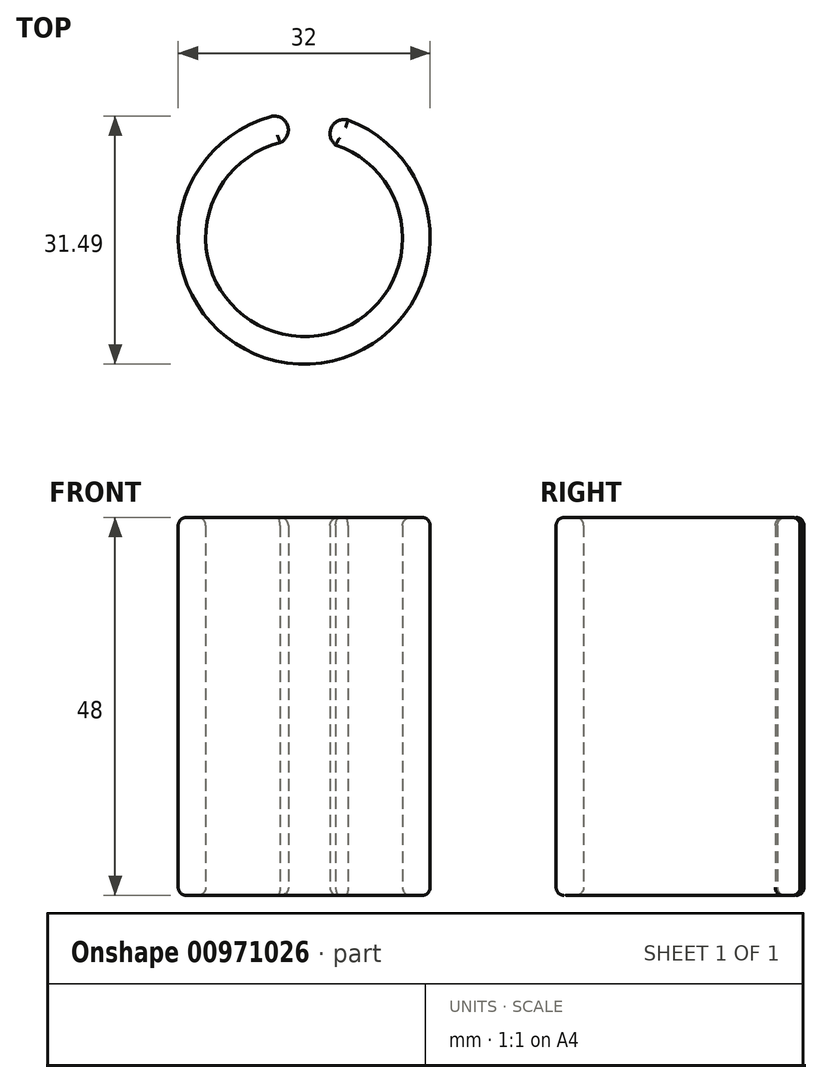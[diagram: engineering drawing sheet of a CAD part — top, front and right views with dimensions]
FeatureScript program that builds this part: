
annotation { "Feature Type Name" : "Feature", "Feature Type Description" : "" }
export const myFeature = defineFeature(function(context is Context, id is Id, definition is map)
    precondition{}
    {
        {
            var Q0;
            Q0=qCreatedBy(makeId("Top.planeOp"),FACE);
            var sketch = newSketch(context, id + "F0", { "sketchPlane" : qUnion([Q0])});
            skArc(sketch, "E0", {"start": v(-3.07, 12.12) * mm, "mid": v(-0.49, -12.5) * mm, "end": v(4, 11.84) * mm});
            skArc(sketch, "E1", {"start": v(-4.23, 15.43) * mm, "mid": v(-0.7, -15.98) * mm, "end": v(5.57, 15) * mm});
            skArc(sketch, "E2", {"start": v(5.57, 15) * mm, "mid": v(3.47, 14.07) * mm, "end": v(4, 11.84) * mm});
            skArc(sketch, "E3", {"start": v(-3.07, 12.12) * mm, "mid": v(-2.1, 14.32) * mm, "end": v(-4.23, 15.43) * mm});
            skSolve(sketch);
        }
        {
            var Q0;
            Q0=makeQuery(id+"F0.imprint","IMPRINT",FACE,{"disambiguationData":[TD([[makeQuery(id+"F0.imprint","IMPRINT",EDGE,{"derivedFrom":sQuery(id+"F0.wireOp",EDGE,"E0")}),-1.0]])]});
            extrude(context, id + "F1", {"entities" : qUnion([Q0]), "depth" : 48 * mm, "offsetDistance" : 25 * mm, "symmetric" : true});
        }
        {
            var Q0;
            Q0=makeQuery(id+"F1.opExtrude","CAP_EDGE",EDGE,{"disambiguationData":[OSD([sQuery(id+"F0.wireOp",EDGE,"E1")])],"isStart":false});
            var Q1;
            Q1=makeQuery(id+"F1.opExtrude","CAP_EDGE",EDGE,{"disambiguationData":[OSD([sQuery(id+"F0.wireOp",EDGE,"E0")])],"isStart":false});
            var Q2;
            Q2=makeQuery(id+"F1.opExtrude","CAP_EDGE",EDGE,{"disambiguationData":[OSD([sQuery(id+"F0.wireOp",EDGE,"E3")])],"isStart":false});
            var Q3;
            Q3=makeQuery(id+"F1.opExtrude","CAP_EDGE",EDGE,{"disambiguationData":[OSD([sQuery(id+"F0.wireOp",EDGE,"E2")])],"isStart":false});
            var Q4;
            Q4=makeQuery(id+"F1.opExtrude","CAP_EDGE",EDGE,{"disambiguationData":[OSD([sQuery(id+"F0.wireOp",EDGE,"E0")])],"isStart":true});
            var Q5;
            Q5=makeQuery(id+"F1.opExtrude","CAP_EDGE",EDGE,{"disambiguationData":[OSD([sQuery(id+"F0.wireOp",EDGE,"E2")])],"isStart":true});
            var Q6;
            Q6=makeQuery(id+"F1.opExtrude","CAP_EDGE",EDGE,{"disambiguationData":[OSD([sQuery(id+"F0.wireOp",EDGE,"E3")])],"isStart":true});
            var Q7;
            Q7=makeQuery(id+"F1.opExtrude","CAP_EDGE",EDGE,{"disambiguationData":[OSD([sQuery(id+"F0.wireOp",EDGE,"E1")])],"isStart":true});
            fillet(context, id + "F2", {"entities" : qUnion([Q0, Q1, Q2, Q3, Q4, Q5, Q6, Q7]), "radius" : 1 * mm, "tangentPropagation" : true, "allowEdgeOverflow" : false});
        }
    });
